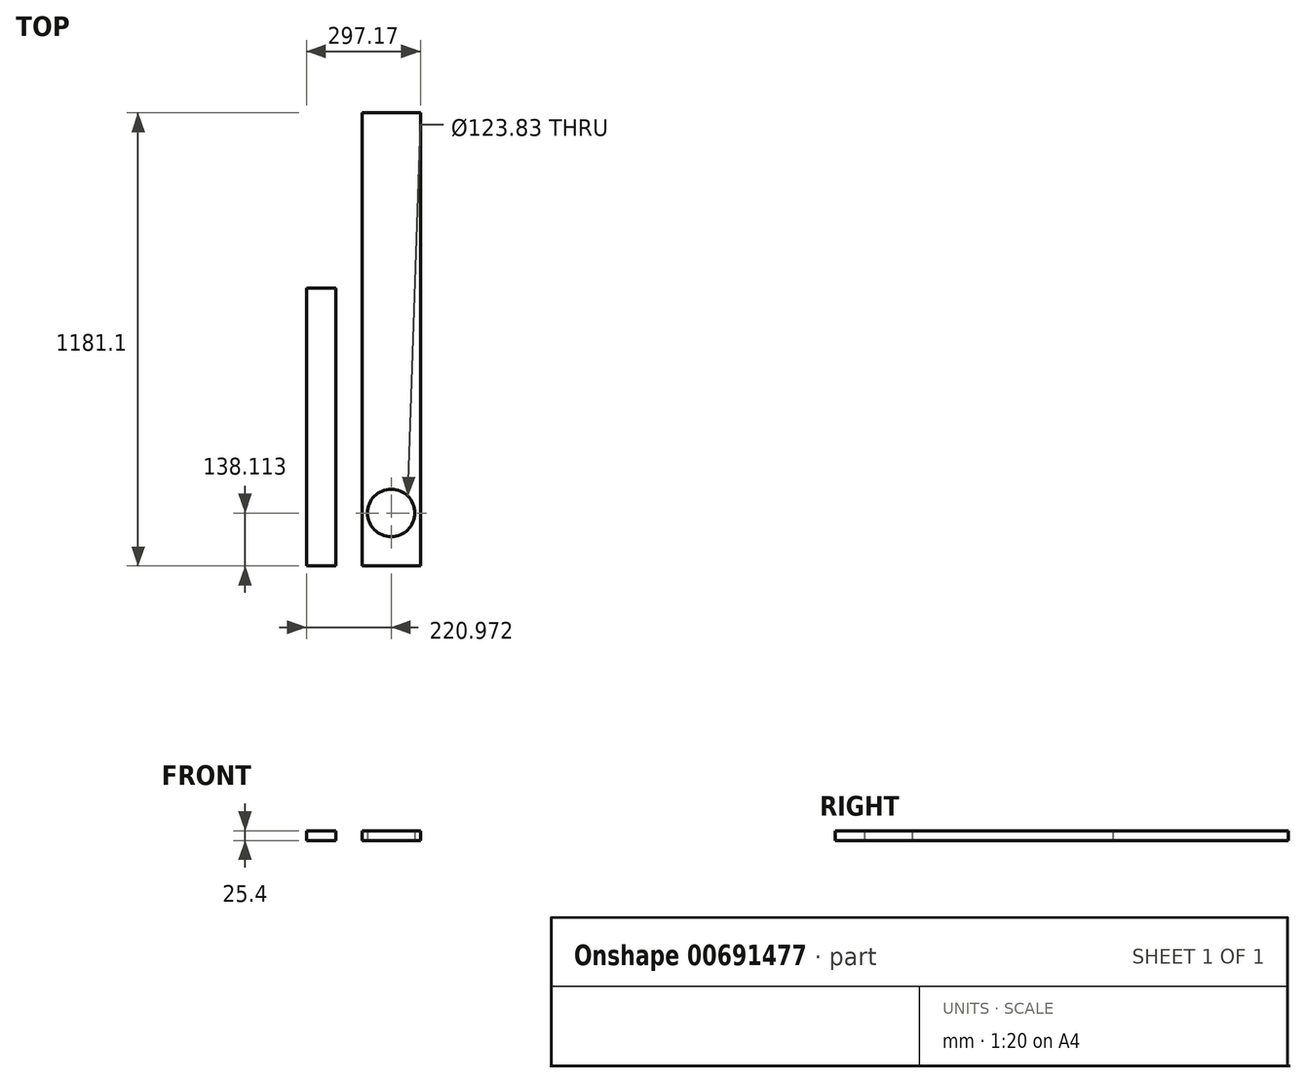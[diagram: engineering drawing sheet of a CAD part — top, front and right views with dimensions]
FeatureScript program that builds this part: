
annotation { "Feature Type Name" : "Feature", "Feature Type Description" : "" }
export const myFeature = defineFeature(function(context is Context, id is Id, definition is map)
    precondition{}
    {
        {
            var Q0;
            Q0=qCreatedBy(makeId("Top.planeOp"),FACE);
            var sketch = newSketch(context, id + "F0", { "sketchPlane" : qUnion([Q0])});
            skLineSegment(sketch, "E0.bottom", {"start": v(0, 0) * mm, "end": v(-76.2, 0) * mm});
            skLineSegment(sketch, "E0.top", {"start": v(0, 723.9) * mm, "end": v(-76.2, 723.9) * mm});
            skLineSegment(sketch, "E0.left", {"start": v(0, 0) * mm, "end": v(0, 723.9) * mm});
            skLineSegment(sketch, "E0.right", {"start": v(-76.2, 0) * mm, "end": v(-76.2, 723.9) * mm});
            skLineSegment(sketch, "E1.bottom", {"start": v(68.57, 0) * mm, "end": v(220.97, 0) * mm});
            skLineSegment(sketch, "E1.top", {"start": v(68.57, 1181.1) * mm, "end": v(220.97, 1181.1) * mm});
            skLineSegment(sketch, "E1.left", {"start": v(68.57, 0) * mm, "end": v(68.57, 1181.1) * mm});
            skLineSegment(sketch, "E1.right", {"start": v(220.97, 0) * mm, "end": v(220.97, 1181.1) * mm});
            skPoint(sketch, "E2", {"position": v(144.77, 0) * mm});
            skPoint(sketch, "E3", {"position": v(144.77, 1181.1) * mm});
            skCircle(sketch, "E4", {"center": v(144.77, 138.11) * mm, "radius": 61.91 * mm});
            skSolve(sketch);
        }
        {
            var Q0;
            Q0=makeQuery(id+"F0.imprint","IMPRINT",FACE,{"disambiguationData":[TD([[makeQuery(id+"F0.imprint","IMPRINT",EDGE,{"derivedFrom":sQuery(id+"F0.wireOp",EDGE,"E1.bottom")}),1.0]])]});
            extrude(context, id + "F1", {"entities" : qUnion([Q0]), "depth" : 6.35 * mm, "offsetDistance" : 25.4 * mm});
        }
        {
            var Q0;
            Q0 = qSketchRegion(id + "F0", true);
            extrude(context, id + "F2", {"entities" : qUnion([Q0]), "operationType" : NewBodyOperationType.ADD, "depth" : 25.4 * mm, "offsetDistance" : 25.4 * mm});
        }
    });
